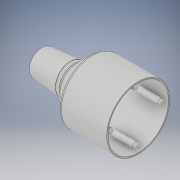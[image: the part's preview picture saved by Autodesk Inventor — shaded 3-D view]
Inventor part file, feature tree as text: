
AUTODESK INVENTOR PART (.ipt)
format: ipt  version: 2019 (Build 230136000, 136)  size: 244,736 bytes
history: native  units: mm
features: fillet x4, sketch x4, extrude x3, revolve x1, plane x1
ambient origin geometry x8: Origin, YZ Plane, XZ Plane, XY Plane, X Axis, Y Axis, Z Axis, Center Point
bodies: Solid1 (feature_tree)
feature tree (13):
  revolve  "Revolution1"  [1 undecoded]
  fillet  "Fillet1"  Radius=9.0mm
  fillet  "Fillet2"  Radius=22.0mm
  plane  "Work Plane1"
  extrude  "Extrusion1"  Depth=22.0mm
  extrude  "Extrusion2"  Depth=2.0mm
  extrude  "Extrusion3"  Depth=2.0mm
  fillet  "Fillet5"  [1 undecoded]
  fillet  "Fillet7"  Radius=1.0mm
  sketch  "Sketch1"  dims[d0=20.0mm d1=0.872665mm d2=9.0mm d3=22.0mm]
  sketch  "Sketch2"  dims[d4=90.0deg d5=22.0mm]
  sketch  "Sketch3"  dims[d6=1.0mm d7=2.0mm]
  sketch  "Sketch4"  dims[d8=2.0mm d9=50.0mm d10=135.0deg d11=1.0mm d12=2.0mm d14=4.0mm d15=0.0mm d16=4.0mm d17=2.0mm d18=2.0mm d19=22.332156mm d21=4.0mm d22=0.0mm d24=2.0mm d25=8.0mm d26=0.0mm d28=4.0mm d29=4.0mm d30=4.0mm d31=20.0mm d32=20.0mm d33=20.0mm d34=20.0mm d35=35.0mm d36=0.0mm d37=36.0mm d38=1.0mm d40=2.0mm]
note: 2 required parameter values undecoded (feature->parameter linkage not recoverable at this tier; creation-order binding heuristic only, values carry confidence <= 0.55)